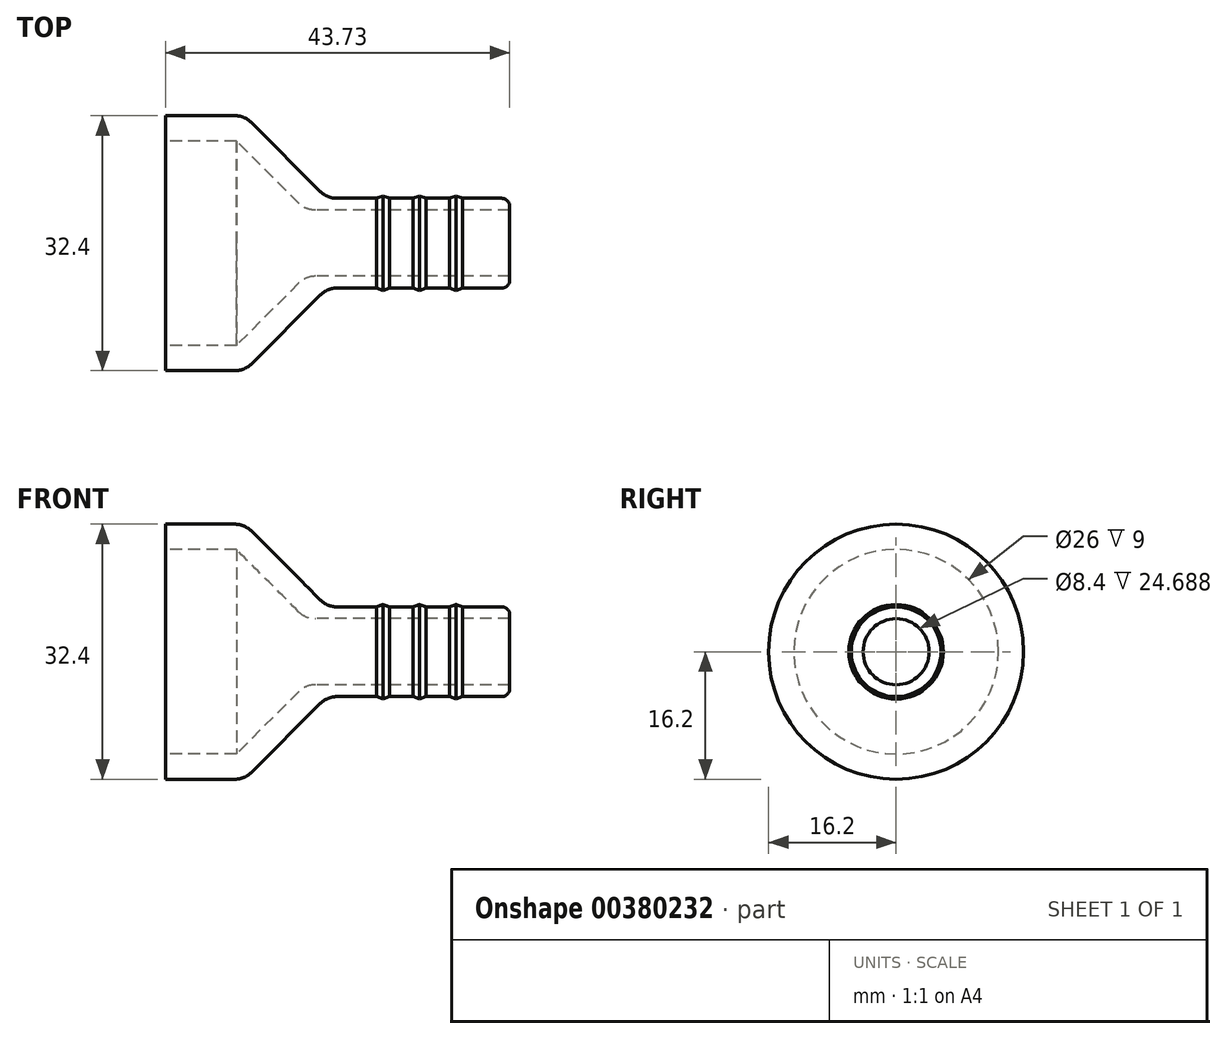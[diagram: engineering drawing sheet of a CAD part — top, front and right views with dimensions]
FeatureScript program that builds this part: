
annotation { "Feature Type Name" : "Feature", "Feature Type Description" : "" }
export const myFeature = defineFeature(function(context is Context, id is Id, definition is map)
    precondition{}
    {
        {
            var Q0;
            Q0=qCreatedBy(makeId("Front.planeOp"),FACE);
            var sketch = newSketch(context, id + "F0", { "sketchPlane" : qUnion([Q0])});
            skLineSegment(sketch, "E0", {"start": v(0, 0) * mm, "end": v(0, 13) * mm});
            skLineSegment(sketch, "E1", {"start": v(43.73, 4.7) * mm, "end": v(43.73, 0) * mm});
            skLineSegment(sketch, "E2", {"start": v(0, 13) * mm, "end": v(9, 13) * mm});
            skLineSegment(sketch, "E3", {"start": v(9, 13) * mm, "end": v(16.92, 5.08) * mm});
            skLineSegment(sketch, "E4", {"start": v(19.04, 4.2) * mm, "end": v(43.73, 4.2) * mm});
            skLineSegment(sketch, "E5", {"start": v(0, 0) * mm, "end": v(43.73, 0) * mm});
            skLineSegment(sketch, "E6", {"start": v(17.8, 4.2) * mm, "end": v(0, 4.2) * mm, "construction": true});
            skLineSegment(sketch, "E7", {"start": v(0, 13) * mm, "end": v(0, 16.2) * mm});
            skLineSegment(sketch, "E8", {"start": v(0, 16.2) * mm, "end": v(8.8, 16.2) * mm});
            skLineSegment(sketch, "E9", {"start": v(10.92, 15.32) * mm, "end": v(19.66, 6.58) * mm});
            skLineSegment(sketch, "E10", {"start": v(26.79, 5.7) * mm, "end": v(27.6, 6) * mm});
            skLineSegment(sketch, "E11", {"start": v(27.6, 6) * mm, "end": v(28.43, 5.7) * mm});
            skLineSegment(sketch, "E12", {"start": v(31.43, 5.7) * mm, "end": v(32.26, 6) * mm});
            skLineSegment(sketch, "E13", {"start": v(32.26, 6) * mm, "end": v(33.08, 5.7) * mm});
            skLineSegment(sketch, "E14", {"start": v(36.08, 5.7) * mm, "end": v(36.9, 6) * mm});
            skLineSegment(sketch, "E15", {"start": v(36.9, 6) * mm, "end": v(37.73, 5.7) * mm});
            skLineSegment(sketch, "E16", {"start": v(26.79, 5.7) * mm, "end": v(28.43, 5.7) * mm, "construction": true});
            skLineSegment(sketch, "E17", {"start": v(31.43, 5.7) * mm, "end": v(33.08, 5.7) * mm, "construction": true});
            skLineSegment(sketch, "E18", {"start": v(36.08, 5.7) * mm, "end": v(37.73, 5.7) * mm, "construction": true});
            skLineSegment(sketch, "E19", {"start": v(21.79, 5.7) * mm, "end": v(26.79, 5.7) * mm});
            skLineSegment(sketch, "E20", {"start": v(28.43, 5.7) * mm, "end": v(31.43, 5.7) * mm});
            skLineSegment(sketch, "E21", {"start": v(33.08, 5.7) * mm, "end": v(36.08, 5.7) * mm});
            skLineSegment(sketch, "E22", {"start": v(37.73, 5.7) * mm, "end": v(42.73, 5.7) * mm});
            skPoint(sketch, "E23.visualSharp", {"position": v(43.73, 5.7) * mm});
            skArc(sketch, "E23.filletArc", {"start": v(43.73, 4.7) * mm, "mid": v(43.44, 5.4) * mm, "end": v(42.73, 5.7) * mm});
            skPoint(sketch, "E24.visualSharp", {"position": v(17.8, 4.2) * mm});
            skArc(sketch, "E24.filletArc", {"start": v(16.92, 5.08) * mm, "mid": v(17.9, 4.43) * mm, "end": v(19.04, 4.2) * mm});
            skPoint(sketch, "E25.visualSharp", {"position": v(20.54, 5.7) * mm});
            skArc(sketch, "E25.filletArc", {"start": v(19.66, 6.58) * mm, "mid": v(20.64, 5.93) * mm, "end": v(21.79, 5.7) * mm});
            skPoint(sketch, "E26.visualSharp", {"position": v(10.04, 16.2) * mm});
            skArc(sketch, "E26.filletArc", {"start": v(10.92, 15.32) * mm, "mid": v(9.95, 15.97) * mm, "end": v(8.8, 16.2) * mm});
            skSolve(sketch);
        }
        {
            var Q0;
            Q0=makeQuery(id+"F0.imprint","IMPRINT",FACE,{"disambiguationData":[TD([[makeQuery(id+"F0.imprint","IMPRINT",EDGE,{"derivedFrom":sQuery(id+"F0.wireOp",EDGE,"E2")}),1.0]])]});
            var Q1;
            Q1=sQuery(id+"F0.wireOp",EDGE,"E5");
            revolve(context, id + "F1", {"entities" : qUnion([Q0]), "axis" : qUnion([Q1]), "revolveType" : RevolveType.FULL});
        }
    });
